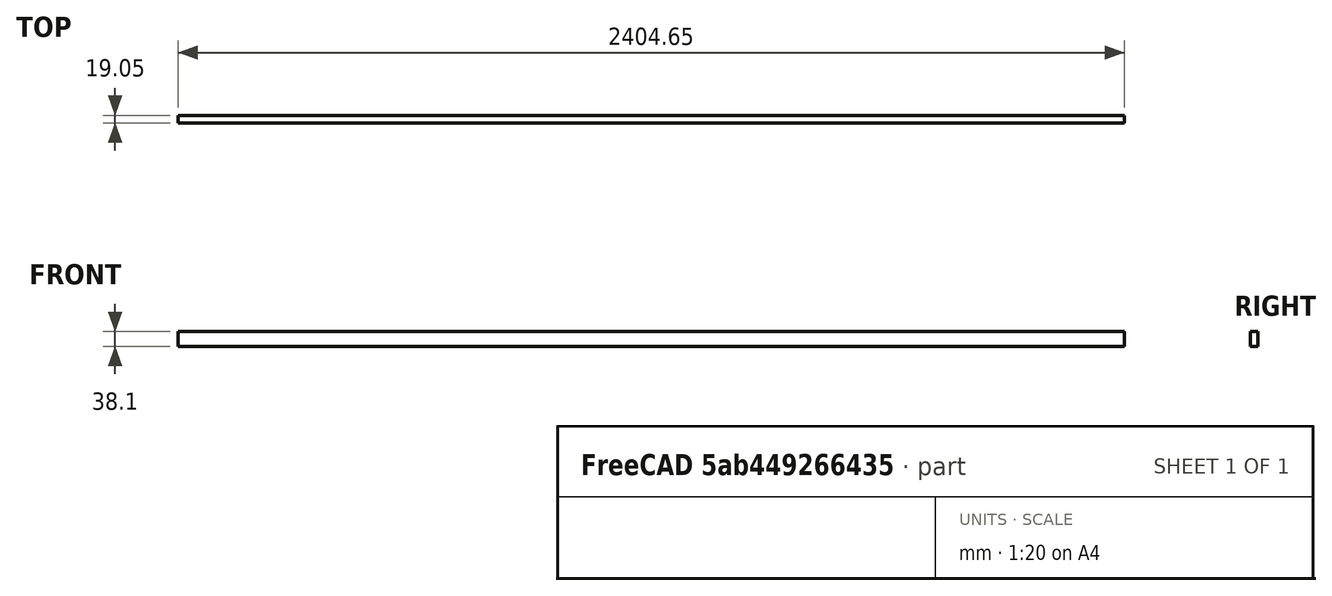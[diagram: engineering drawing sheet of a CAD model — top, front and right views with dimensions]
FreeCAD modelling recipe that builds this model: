
FCSTD DOCUMENT  (FreeCAD 0.20R29177 (Git))
Label: topLeftFrontBand
License: All rights reserved
LicenseURL: http://en.wikipedia.org/wiki/All_rights_reserved
objects: Sketcher::SketchObject×1, PartDesign::Pad×1, PartDesign::Body×1
note: 4 computed .brp shape members not serialized (recipe doc carries the construction recipe); baked Part::Feature solids carry a one-line shape summary decoded from their .brp

FEATURE [Sketcher::SketchObject] Sketch
  FullyConstrained = true
  MapMode = 5
  Placement = pos=(0,0,0) rot=(1,0,0;1.5708rad)
  Support = -> [XZ_Plane001]
  expr: Constraints[10] = 1.5 * 25.4
  expr: Constraints[9] = 2404.65
  sketch-geometry (4):
    g0: LineSegment StartX=0 StartY=0 StartZ=0 EndX=2404.65 EndY=0 EndZ=0
    g1: LineSegment StartX=2404.65 StartY=0 StartZ=0 EndX=2404.65 EndY=38.1 EndZ=0
    g2: LineSegment StartX=2404.65 StartY=38.1 StartZ=0 EndX=0 EndY=38.1 EndZ=0
    g3: LineSegment StartX=0 StartY=38.1 StartZ=0 EndX=0 EndY=0 EndZ=0
  constraints (11):
    c: Coincident(g0,g1)
    c: Coincident(g1,g2)
    c: Coincident(g2,g3)
    c: Coincident(g3,g0)
    c: Horizontal(g0)
    c: Horizontal(g2)
    c: Vertical(g1)
    c: Vertical(g3)
    c: Coincident(g0,g-1)
    c: DistanceX(g0,g0) = 2404.65
    c: DistanceY(g3,g3) = 38.1
FEATURE [PartDesign::Pad] Pad
  Direction = (0,-1,-2e-16)
  Length = 19.05
  Length2 = 10
  Placement = pos=(0,0,0) rot=(1,0,0;1.5708rad)
  Profile = -> Sketch
  ReferenceAxis = -> Sketch [N_Axis]
  Type = 0
  expr: Length = 3 / 4 * 25.4
FEATURE [PartDesign::Body] Body001
  Group = -> [Sketch,Pad]
  Origin = -> Origin001
  Tip = -> Pad
